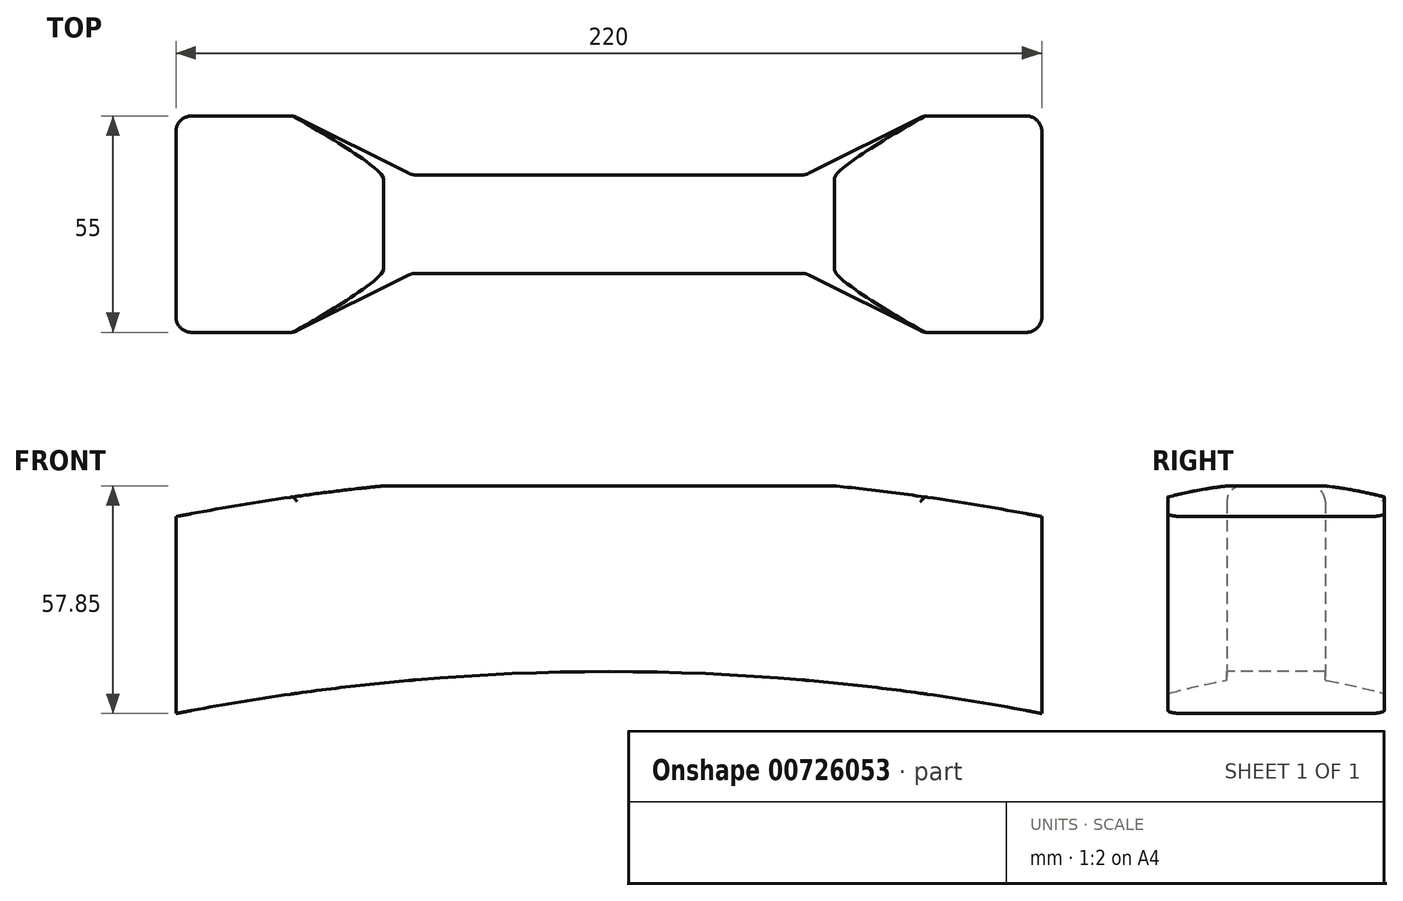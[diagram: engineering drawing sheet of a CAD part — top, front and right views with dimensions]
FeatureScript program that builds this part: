
annotation { "Feature Type Name" : "Feature", "Feature Type Description" : "" }
export const myFeature = defineFeature(function(context is Context, id is Id, definition is map)
    precondition{}
    {
        {
            var Q0;
            Q0=qCreatedBy(makeId("Top.planeOp"),FACE);
            var sketch = newSketch(context, id + "F0", { "sketchPlane" : qUnion([Q0])});
            skPoint(sketch, "E0.middle", {"position": v(0, 0) * mm});
            skPoint(sketch, "E0.left.end.orphan", {"position": v(50, 17.5) * mm});
            skPoint(sketch, "E1.orphan", {"position": v(50, -17.5) * mm});
            skLineSegment(sketch, "E2.0", {"start": v(-80, 27.5) * mm, "end": v(-110, 27.5) * mm});
            skLineSegment(sketch, "E3.0", {"start": v(-80, -27.5) * mm, "end": v(-110, -27.5) * mm});
            skLineSegment(sketch, "E4", {"start": v(-110, 27.5) * mm, "end": v(-110, -27.5) * mm});
            skPoint(sketch, "E5.orphan", {"position": v(-50, 27.5) * mm});
            skLineSegment(sketch, "E6.0", {"start": v(0, -12.5) * mm, "end": v(-50, -12.5) * mm});
            skLineSegment(sketch, "E7.0", {"start": v(0, 12.5) * mm, "end": v(-50, 12.5) * mm});
            skPoint(sketch, "E8.orphan", {"position": v(0, -17.5) * mm});
            skPoint(sketch, "E9.orphan", {"position": v(0, 17.5) * mm});
            skPoint(sketch, "E10.start.orphan", {"position": v(-50, -17.5) * mm});
            skPoint(sketch, "E11.end.orphan", {"position": v(-50, 17.5) * mm});
            skLineSegment(sketch, "E12", {"start": v(-80, -27.5) * mm, "end": v(-50, -12.5) * mm});
            skLineSegment(sketch, "E13", {"start": v(-50, 12.5) * mm, "end": v(-80, 27.5) * mm});
            skLineSegment(sketch, "E14.MirrorCS", {"start": v(80, -27.5) * mm, "end": v(50, -12.5) * mm});
            skLineSegment(sketch, "E15.MirrorCS", {"start": v(80, -27.5) * mm, "end": v(110, -27.5) * mm});
            skLineSegment(sketch, "E16.MirrorCS", {"start": v(0, -12.5) * mm, "end": v(50, -12.5) * mm});
            skLineSegment(sketch, "E17.MirrorCS", {"start": v(0, 12.5) * mm, "end": v(50, 12.5) * mm});
            skLineSegment(sketch, "E18.MirrorCS", {"start": v(50, 12.5) * mm, "end": v(80, 27.5) * mm});
            skLineSegment(sketch, "E19.MirrorCS", {"start": v(110, 27.5) * mm, "end": v(110, -27.5) * mm});
            skLineSegment(sketch, "E20.MirrorCS", {"start": v(80, 27.5) * mm, "end": v(110, 27.5) * mm});
            skSolve(sketch);
        }
        {
            var Q0;
            Q0=makeQuery(id+"F0.imprint","IMPRINT",FACE,{"disambiguationData":[TD([[makeQuery(id+"F0.imprint","IMPRINT",EDGE,{"derivedFrom":sQuery(id+"F0.wireOp",EDGE,"E2.0")}),1.0]])]});
            extrude(context, id + "F1", {"entities" : qUnion([Q0]), "depth" : 100 * mm, "offsetDistance" : 25 * mm});
        }
        {
            var Q0;
            Q0=makeQuery(id+"F1.opExtrude","SWEPT_FACE",FACE,{"disambiguationData":[OSD([sQuery(id+"F0.wireOp",EDGE,"E3.0")])]});
            var sketch = newSketch(context, id + "F2", { "sketchPlane" : qUnion([Q0])});
            skPoint(sketch, "E21.orphan", {"position": v(125.12, 0) * mm});
            skLineSegment(sketch, "E22.left", {"start": v(150, 32.82) * mm, "end": v(150, 82.82) * mm});
            skLineSegment(sketch, "E22.right", {"start": v(-150, 32.82) * mm, "end": v(-150, 82.82) * mm});
            skPoint(sketch, "E22.middle", {"position": v(0, 57.82) * mm});
            skArc(sketch, "E23", {"start": v(8.21, 102.82) * mm, "mid": v(0, 102.88) * mm, "end": v(-8.21, 102.82) * mm});
            skArc(sketch, "E24", {"start": v(150, 82.82) * mm, "mid": v(75.67, 97.84) * mm, "end": v(0, 102.88) * mm});
            skLineSegment(sketch, "E25", {"start": v(0, 57.82) * mm, "end": v(0, 52.82) * mm});
            skPoint(sketch, "E26.orphan", {"position": v(-150, 12.82) * mm});
            skPoint(sketch, "E27.0.start.orphan", {"position": v(150, 12.82) * mm});
            skPoint(sketch, "E28.orphan", {"position": v(0, 12.82) * mm});
            skArc(sketch, "E29", {"start": v(150, 32.82) * mm, "mid": v(0, 52.82) * mm, "end": v(-150, 32.82) * mm});
            skPoint(sketch, "E30.start.orphan", {"position": v(0, 102.88) * mm});
            skArc(sketch, "E31.trimOffspring", {"start": v(-8.21, 102.82) * mm, "mid": v(-79.74, 97.28) * mm, "end": v(-150, 82.82) * mm});
            skPoint(sketch, "E32.orphan", {"position": v(0, 32.82) * mm});
            skSolve(sketch);
        }
        {
            var Q0;
            Q0 = qSketchRegion(id + "F2", true);
            extrude(context, id + "F3", {"entities" : qUnion([Q0]), "operationType" : NewBodyOperationType.INTERSECT, "oppositeDirection" : true, "depth" : 185 * mm, "offsetDistance" : 25 * mm});
        }
        {
            var Q0;
            Q0=makeQuery(id+"F1.opExtrude","CAP_EDGE",EDGE,{"disambiguationData":[OSD([sQuery(id+"F0.wireOp",EDGE,"E7.0"),sQuery(id+"F0.wireOp",EDGE,"E17.MirrorCS")])],"isStart":false});
            var Q1;
            Q1=makeQuery(id+"F3.boolean.opBoolean","INTERSECT",EDGE,{"derivedFrom":[makeQuery(id+"F1.opExtrude","SWEPT_FACE",FACE,{"disambiguationData":[OSD([sQuery(id+"F0.wireOp",EDGE,"E18.MirrorCS")])]}),makeQuery(id+"F3.boolean.toolComplement.opBoolean","COPY",FACE,{"derivedFrom":makeQuery(id+"F3.opExtrude","SWEPT_FACE",FACE,{"disambiguationData":[OSD([sQuery(id+"F2.wireOp",EDGE,"E23"),sQuery(id+"F2.wireOp",EDGE,"E24"),sQuery(id+"F2.wireOp",EDGE,"E31.trimOffspring")])]})})]});
            var Q2;
            Q2=makeQuery(id+"F1.opExtrude","CAP_EDGE",EDGE,{"disambiguationData":[OSD([sQuery(id+"F0.wireOp",EDGE,"E18.MirrorCS")])],"isStart":false});
            var Q3;
            Q3=makeQuery(id+"F1.opExtrude","SWEPT_EDGE",EDGE,{"disambiguationData":[OSD([sQuery(id+"F0.wireOp",EDGE,"E17.MirrorCS"),sQuery(id+"F0.wireOp",EDGE,"E18.MirrorCS")])]});
            var Q4;
            Q4=makeQuery(id+"F1.opExtrude","SWEPT_EDGE",EDGE,{"disambiguationData":[OSD([sQuery(id+"F0.wireOp",EDGE,"E18.MirrorCS"),sQuery(id+"F0.wireOp",EDGE,"E20.MirrorCS")])]});
            var Q5;
            Q5=makeQuery(id+"F3.boolean.opBoolean","INTERSECT",EDGE,{"derivedFrom":[makeQuery(id+"F1.opExtrude","SWEPT_FACE",FACE,{"disambiguationData":[OSD([sQuery(id+"F0.wireOp",EDGE,"E20.MirrorCS")])]}),makeQuery(id+"F3.boolean.toolComplement.opBoolean","COPY",FACE,{"derivedFrom":makeQuery(id+"F3.opExtrude","SWEPT_FACE",FACE,{"disambiguationData":[OSD([sQuery(id+"F2.wireOp",EDGE,"E23"),sQuery(id+"F2.wireOp",EDGE,"E24"),sQuery(id+"F2.wireOp",EDGE,"E31.trimOffspring")])]})})]});
            var Q6;
            Q6=makeQuery(id+"F1.opExtrude","SWEPT_EDGE",EDGE,{"disambiguationData":[OSD([sQuery(id+"F0.wireOp",EDGE,"E19.MirrorCS"),sQuery(id+"F0.wireOp",EDGE,"E20.MirrorCS")])]});
            var Q7;
            Q7=makeQuery(id+"F3.boolean.opBoolean","INTERSECT",EDGE,{"derivedFrom":[makeQuery(id+"F1.opExtrude","SWEPT_FACE",FACE,{"disambiguationData":[OSD([sQuery(id+"F0.wireOp",EDGE,"E19.MirrorCS")])]}),makeQuery(id+"F3.boolean.toolComplement.opBoolean","COPY",FACE,{"derivedFrom":makeQuery(id+"F3.opExtrude","SWEPT_FACE",FACE,{"disambiguationData":[OSD([sQuery(id+"F2.wireOp",EDGE,"E23"),sQuery(id+"F2.wireOp",EDGE,"E24"),sQuery(id+"F2.wireOp",EDGE,"E31.trimOffspring")])]})})]});
            var Q8;
            Q8=makeQuery(id+"F3.boolean.opBoolean","INTERSECT",EDGE,{"derivedFrom":[makeQuery(id+"F1.opExtrude","SWEPT_FACE",FACE,{"disambiguationData":[OSD([sQuery(id+"F0.wireOp",EDGE,"E19.MirrorCS")])]}),makeQuery(id+"F3.boolean.toolComplement.opBoolean","COPY",FACE,{"derivedFrom":makeQuery(id+"F3.opExtrude","SWEPT_FACE",FACE,{"disambiguationData":[OSD([sQuery(id+"F2.wireOp",EDGE,"E29")])]})})]});
            var Q9;
            Q9=makeQuery(id+"F1.opExtrude","SWEPT_EDGE",EDGE,{"disambiguationData":[OSD([sQuery(id+"F0.wireOp",EDGE,"E15.MirrorCS"),sQuery(id+"F0.wireOp",EDGE,"E19.MirrorCS")])]});
            var Q10;
            Q10=makeQuery(id+"F3.boolean.opBoolean","INTERSECT",EDGE,{"derivedFrom":[makeQuery(id+"F1.opExtrude","SWEPT_FACE",FACE,{"disambiguationData":[OSD([sQuery(id+"F0.wireOp",EDGE,"E20.MirrorCS")])]}),makeQuery(id+"F3.boolean.toolComplement.opBoolean","COPY",FACE,{"derivedFrom":makeQuery(id+"F3.opExtrude","SWEPT_FACE",FACE,{"disambiguationData":[OSD([sQuery(id+"F2.wireOp",EDGE,"E29")])]})})]});
            var Q11;
            Q11=makeQuery(id+"F3.boolean.opBoolean","INTERSECT",EDGE,{"derivedFrom":[makeQuery(id+"F1.opExtrude","SWEPT_FACE",FACE,{"disambiguationData":[OSD([sQuery(id+"F0.wireOp",EDGE,"E18.MirrorCS")])]}),makeQuery(id+"F3.boolean.toolComplement.opBoolean","COPY",FACE,{"derivedFrom":makeQuery(id+"F3.opExtrude","SWEPT_FACE",FACE,{"disambiguationData":[OSD([sQuery(id+"F2.wireOp",EDGE,"E29")])]})})]});
            var Q12;
            Q12=makeQuery(id+"F3.boolean.opBoolean","INTERSECT",EDGE,{"derivedFrom":[makeQuery(id+"F1.opExtrude","SWEPT_FACE",FACE,{"disambiguationData":[OSD([sQuery(id+"F0.wireOp",EDGE,"E7.0"),sQuery(id+"F0.wireOp",EDGE,"E17.MirrorCS")])]}),makeQuery(id+"F3.boolean.toolComplement.opBoolean","COPY",FACE,{"derivedFrom":makeQuery(id+"F3.opExtrude","SWEPT_FACE",FACE,{"disambiguationData":[OSD([sQuery(id+"F2.wireOp",EDGE,"E29")])]})})]});
            var Q13;
            Q13=makeQuery(id+"F1.opExtrude","SWEPT_EDGE",EDGE,{"disambiguationData":[OSD([sQuery(id+"F0.wireOp",EDGE,"E7.0"),sQuery(id+"F0.wireOp",EDGE,"E13")])]});
            var Q14;
            Q14=makeQuery(id+"F3.boolean.opBoolean","INTERSECT",EDGE,{"derivedFrom":[makeQuery(id+"F1.opExtrude","SWEPT_FACE",FACE,{"disambiguationData":[OSD([sQuery(id+"F0.wireOp",EDGE,"E13")])]}),makeQuery(id+"F3.boolean.toolComplement.opBoolean","COPY",FACE,{"derivedFrom":makeQuery(id+"F3.opExtrude","SWEPT_FACE",FACE,{"disambiguationData":[OSD([sQuery(id+"F2.wireOp",EDGE,"E23"),sQuery(id+"F2.wireOp",EDGE,"E24"),sQuery(id+"F2.wireOp",EDGE,"E31.trimOffspring")])]})})]});
            var Q15;
            Q15=makeQuery(id+"F1.opExtrude","CAP_EDGE",EDGE,{"disambiguationData":[OSD([sQuery(id+"F0.wireOp",EDGE,"E13")])],"isStart":false});
            var Q16;
            Q16=makeQuery(id+"F3.boolean.opBoolean","INTERSECT",EDGE,{"derivedFrom":[makeQuery(id+"F1.opExtrude","SWEPT_FACE",FACE,{"disambiguationData":[OSD([sQuery(id+"F0.wireOp",EDGE,"E13")])]}),makeQuery(id+"F3.boolean.toolComplement.opBoolean","COPY",FACE,{"derivedFrom":makeQuery(id+"F3.opExtrude","SWEPT_FACE",FACE,{"disambiguationData":[OSD([sQuery(id+"F2.wireOp",EDGE,"E29")])]})})]});
            var Q17;
            Q17=makeQuery(id+"F1.opExtrude","SWEPT_EDGE",EDGE,{"disambiguationData":[OSD([sQuery(id+"F0.wireOp",EDGE,"E2.0"),sQuery(id+"F0.wireOp",EDGE,"E13")])]});
            var Q18;
            Q18=makeQuery(id+"F3.boolean.opBoolean","INTERSECT",EDGE,{"derivedFrom":[makeQuery(id+"F1.opExtrude","SWEPT_FACE",FACE,{"disambiguationData":[OSD([sQuery(id+"F0.wireOp",EDGE,"E2.0")])]}),makeQuery(id+"F3.boolean.toolComplement.opBoolean","COPY",FACE,{"derivedFrom":makeQuery(id+"F3.opExtrude","SWEPT_FACE",FACE,{"disambiguationData":[OSD([sQuery(id+"F2.wireOp",EDGE,"E23"),sQuery(id+"F2.wireOp",EDGE,"E24"),sQuery(id+"F2.wireOp",EDGE,"E31.trimOffspring")])]})})]});
            var Q19;
            Q19=makeQuery(id+"F3.boolean.opBoolean","INTERSECT",EDGE,{"derivedFrom":[makeQuery(id+"F1.opExtrude","SWEPT_FACE",FACE,{"disambiguationData":[OSD([sQuery(id+"F0.wireOp",EDGE,"E2.0")])]}),makeQuery(id+"F3.boolean.toolComplement.opBoolean","COPY",FACE,{"derivedFrom":makeQuery(id+"F3.opExtrude","SWEPT_FACE",FACE,{"disambiguationData":[OSD([sQuery(id+"F2.wireOp",EDGE,"E29")])]})})]});
            var Q20;
            Q20=makeQuery(id+"F1.opExtrude","SWEPT_EDGE",EDGE,{"disambiguationData":[OSD([sQuery(id+"F0.wireOp",EDGE,"E2.0"),sQuery(id+"F0.wireOp",EDGE,"E4")])]});
            var Q21;
            Q21=makeQuery(id+"F3.boolean.opBoolean","INTERSECT",EDGE,{"derivedFrom":[makeQuery(id+"F1.opExtrude","SWEPT_FACE",FACE,{"disambiguationData":[OSD([sQuery(id+"F0.wireOp",EDGE,"E4")])]}),makeQuery(id+"F3.boolean.toolComplement.opBoolean","COPY",FACE,{"derivedFrom":makeQuery(id+"F3.opExtrude","SWEPT_FACE",FACE,{"disambiguationData":[OSD([sQuery(id+"F2.wireOp",EDGE,"E23"),sQuery(id+"F2.wireOp",EDGE,"E24"),sQuery(id+"F2.wireOp",EDGE,"E31.trimOffspring")])]})})]});
            var Q22;
            Q22=makeQuery(id+"F3.boolean.opBoolean","INTERSECT",EDGE,{"derivedFrom":[makeQuery(id+"F1.opExtrude","SWEPT_FACE",FACE,{"disambiguationData":[OSD([sQuery(id+"F0.wireOp",EDGE,"E4")])]}),makeQuery(id+"F3.boolean.toolComplement.opBoolean","COPY",FACE,{"derivedFrom":makeQuery(id+"F3.opExtrude","SWEPT_FACE",FACE,{"disambiguationData":[OSD([sQuery(id+"F2.wireOp",EDGE,"E29")])]})})]});
            var Q23;
            Q23=makeQuery(id+"F1.opExtrude","SWEPT_EDGE",EDGE,{"disambiguationData":[OSD([sQuery(id+"F0.wireOp",EDGE,"E3.0"),sQuery(id+"F0.wireOp",EDGE,"E4")])]});
            var Q24;
            {var subQ0=sQuery(id+"F2.wireOp",EDGE,"E31.trimOffspring");var subQ1=sQuery(id+"F2.wireOp",EDGE,"E24");var subQ2=sQuery(id+"F2.wireOp",EDGE,"E23");Q24=makeQuery(id+"F3.boolean.opBoolean","COPY",EDGE,{"disambiguationData":[topologyDisambiguationEdgeConnected([makeQuery(id+"F1.opExtrude","SWEPT_FACE",FACE,{"disambiguationData":[OSD([sQuery(id+"F0.wireOp",EDGE,"E3.0")])]})])],"derivedFrom":makeQuery(id+"F3.boolean.toolComplement.opBoolean","COPY",EDGE,{"derivedFrom":makeQuery(id+"F3.opExtrude","CAP_EDGE",EDGE,{"disambiguationData":[OSD([subQ2,subQ1,subQ0])],"isStart":true})})});}
            var Q25;
            Q25=makeQuery(id+"F3.boolean.opBoolean","INTERSECT",EDGE,{"derivedFrom":[makeQuery(id+"F1.opExtrude","SWEPT_FACE",FACE,{"disambiguationData":[OSD([sQuery(id+"F0.wireOp",EDGE,"E12")])]}),makeQuery(id+"F3.boolean.toolComplement.opBoolean","COPY",FACE,{"derivedFrom":makeQuery(id+"F3.opExtrude","SWEPT_FACE",FACE,{"disambiguationData":[OSD([sQuery(id+"F2.wireOp",EDGE,"E23"),sQuery(id+"F2.wireOp",EDGE,"E24"),sQuery(id+"F2.wireOp",EDGE,"E31.trimOffspring")])]})})]});
            var Q26;
            Q26=makeQuery(id+"F1.opExtrude","CAP_EDGE",EDGE,{"disambiguationData":[OSD([sQuery(id+"F0.wireOp",EDGE,"E12")])],"isStart":false});
            var Q27;
            Q27=makeQuery(id+"F1.opExtrude","CAP_EDGE",EDGE,{"disambiguationData":[OSD([sQuery(id+"F0.wireOp",EDGE,"E6.0"),sQuery(id+"F0.wireOp",EDGE,"E16.MirrorCS")])],"isStart":false});
            var Q28;
            Q28=makeQuery(id+"F1.opExtrude","SWEPT_EDGE",EDGE,{"disambiguationData":[OSD([sQuery(id+"F0.wireOp",EDGE,"E14.MirrorCS"),sQuery(id+"F0.wireOp",EDGE,"E16.MirrorCS")])]});
            var Q29;
            Q29=makeQuery(id+"F3.boolean.opBoolean","INTERSECT",EDGE,{"derivedFrom":[makeQuery(id+"F1.opExtrude","SWEPT_FACE",FACE,{"disambiguationData":[OSD([sQuery(id+"F0.wireOp",EDGE,"E14.MirrorCS")])]}),makeQuery(id+"F3.boolean.toolComplement.opBoolean","COPY",FACE,{"derivedFrom":makeQuery(id+"F3.opExtrude","SWEPT_FACE",FACE,{"disambiguationData":[OSD([sQuery(id+"F2.wireOp",EDGE,"E23"),sQuery(id+"F2.wireOp",EDGE,"E24"),sQuery(id+"F2.wireOp",EDGE,"E31.trimOffspring")])]})})]});
            var Q30;
            Q30=makeQuery(id+"F1.opExtrude","CAP_EDGE",EDGE,{"disambiguationData":[OSD([sQuery(id+"F0.wireOp",EDGE,"E14.MirrorCS")])],"isStart":false});
            var Q31;
            Q31=makeQuery(id+"F1.opExtrude","SWEPT_EDGE",EDGE,{"disambiguationData":[OSD([sQuery(id+"F0.wireOp",EDGE,"E14.MirrorCS"),sQuery(id+"F0.wireOp",EDGE,"E15.MirrorCS")])]});
            var Q32;
            {var subQ0=sQuery(id+"F2.wireOp",EDGE,"E31.trimOffspring");var subQ1=sQuery(id+"F2.wireOp",EDGE,"E24");var subQ2=sQuery(id+"F2.wireOp",EDGE,"E23");Q32=makeQuery(id+"F3.boolean.opBoolean","COPY",EDGE,{"disambiguationData":[topologyDisambiguationEdgeConnected([makeQuery(id+"F1.opExtrude","SWEPT_FACE",FACE,{"disambiguationData":[OSD([sQuery(id+"F0.wireOp",EDGE,"E15.MirrorCS")])]})])],"derivedFrom":makeQuery(id+"F3.boolean.toolComplement.opBoolean","COPY",EDGE,{"derivedFrom":makeQuery(id+"F3.opExtrude","CAP_EDGE",EDGE,{"disambiguationData":[OSD([subQ2,subQ1,subQ0])],"isStart":true})})});}
            var Q33;
            Q33=makeQuery(id+"F3.boolean.opBoolean","INTERSECT",EDGE,{"derivedFrom":[makeQuery(id+"F1.opExtrude","SWEPT_FACE",FACE,{"disambiguationData":[OSD([sQuery(id+"F0.wireOp",EDGE,"E14.MirrorCS")])]}),makeQuery(id+"F3.boolean.toolComplement.opBoolean","COPY",FACE,{"derivedFrom":makeQuery(id+"F3.opExtrude","SWEPT_FACE",FACE,{"disambiguationData":[OSD([sQuery(id+"F2.wireOp",EDGE,"E29")])]})})]});
            var Q34;
            {var subQ0=sQuery(id+"F2.wireOp",EDGE,"E29");Q34=makeQuery(id+"F3.boolean.opBoolean","COPY",EDGE,{"disambiguationData":[topologyDisambiguationEdgeConnected([makeQuery(id+"F1.opExtrude","SWEPT_FACE",FACE,{"disambiguationData":[OSD([sQuery(id+"F0.wireOp",EDGE,"E15.MirrorCS")])]})])],"derivedFrom":makeQuery(id+"F3.boolean.toolComplement.opBoolean","COPY",EDGE,{"derivedFrom":makeQuery(id+"F3.opExtrude","CAP_EDGE",EDGE,{"disambiguationData":[OSD([subQ0])],"isStart":true})})});}
            var Q35;
            Q35=makeQuery(id+"F3.boolean.opBoolean","INTERSECT",EDGE,{"derivedFrom":[makeQuery(id+"F1.opExtrude","SWEPT_FACE",FACE,{"disambiguationData":[OSD([sQuery(id+"F0.wireOp",EDGE,"E6.0"),sQuery(id+"F0.wireOp",EDGE,"E16.MirrorCS")])]}),makeQuery(id+"F3.boolean.toolComplement.opBoolean","COPY",FACE,{"derivedFrom":makeQuery(id+"F3.opExtrude","SWEPT_FACE",FACE,{"disambiguationData":[OSD([sQuery(id+"F2.wireOp",EDGE,"E29")])]})})]});
            var Q36;
            Q36=makeQuery(id+"F3.boolean.opBoolean","INTERSECT",EDGE,{"derivedFrom":[makeQuery(id+"F1.opExtrude","SWEPT_FACE",FACE,{"disambiguationData":[OSD([sQuery(id+"F0.wireOp",EDGE,"E12")])]}),makeQuery(id+"F3.boolean.toolComplement.opBoolean","COPY",FACE,{"derivedFrom":makeQuery(id+"F3.opExtrude","SWEPT_FACE",FACE,{"disambiguationData":[OSD([sQuery(id+"F2.wireOp",EDGE,"E29")])]})})]});
            var Q37;
            Q37=makeQuery(id+"F1.opExtrude","SWEPT_EDGE",EDGE,{"disambiguationData":[OSD([sQuery(id+"F0.wireOp",EDGE,"E3.0"),sQuery(id+"F0.wireOp",EDGE,"E12")])]});
            var Q38;
            {var subQ0=sQuery(id+"F2.wireOp",EDGE,"E29");Q38=makeQuery(id+"F3.boolean.opBoolean","COPY",EDGE,{"disambiguationData":[topologyDisambiguationEdgeConnected([makeQuery(id+"F1.opExtrude","SWEPT_FACE",FACE,{"disambiguationData":[OSD([sQuery(id+"F0.wireOp",EDGE,"E3.0")])]})])],"derivedFrom":makeQuery(id+"F3.boolean.toolComplement.opBoolean","COPY",EDGE,{"derivedFrom":makeQuery(id+"F3.opExtrude","CAP_EDGE",EDGE,{"disambiguationData":[OSD([subQ0])],"isStart":true})})});}
            var Q39;
            Q39=makeQuery(id+"F1.opExtrude","SWEPT_EDGE",EDGE,{"disambiguationData":[OSD([sQuery(id+"F0.wireOp",EDGE,"E6.0"),sQuery(id+"F0.wireOp",EDGE,"E12")])]});
            var Q40;
            Q40=makeQuery(id+"F3.boolean.opBoolean","INTERSECT",EDGE,{"disambiguationData":[OD(1.0)],"derivedFrom":[makeQuery(id+"F1.opExtrude","CAP_FACE",FACE,{"disambiguationData":[OSD([sQuery(id+"F0.wireOp",EDGE,"E2.0"),sQuery(id+"F0.wireOp",EDGE,"E3.0"),sQuery(id+"F0.wireOp",EDGE,"E4"),sQuery(id+"F0.wireOp",EDGE,"E6.0"),sQuery(id+"F0.wireOp",EDGE,"E7.0"),sQuery(id+"F0.wireOp",EDGE,"E12"),sQuery(id+"F0.wireOp",EDGE,"E13"),sQuery(id+"F0.wireOp",EDGE,"E14.MirrorCS"),sQuery(id+"F0.wireOp",EDGE,"E15.MirrorCS"),sQuery(id+"F0.wireOp",EDGE,"E16.MirrorCS"),sQuery(id+"F0.wireOp",EDGE,"E17.MirrorCS"),sQuery(id+"F0.wireOp",EDGE,"E18.MirrorCS"),sQuery(id+"F0.wireOp",EDGE,"E19.MirrorCS"),sQuery(id+"F0.wireOp",EDGE,"E20.MirrorCS")])],"isStart":false}),makeQuery(id+"F3.boolean.toolComplement.opBoolean","COPY",FACE,{"derivedFrom":makeQuery(id+"F3.opExtrude","SWEPT_FACE",FACE,{"disambiguationData":[OSD([sQuery(id+"F2.wireOp",EDGE,"E23"),sQuery(id+"F2.wireOp",EDGE,"E24"),sQuery(id+"F2.wireOp",EDGE,"E31.trimOffspring")])]})})]});
            var Q41;
            Q41=makeQuery(id+"F3.boolean.opBoolean","INTERSECT",EDGE,{"disambiguationData":[OD(0.0)],"derivedFrom":[makeQuery(id+"F1.opExtrude","CAP_FACE",FACE,{"disambiguationData":[OSD([sQuery(id+"F0.wireOp",EDGE,"E2.0"),sQuery(id+"F0.wireOp",EDGE,"E3.0"),sQuery(id+"F0.wireOp",EDGE,"E4"),sQuery(id+"F0.wireOp",EDGE,"E6.0"),sQuery(id+"F0.wireOp",EDGE,"E7.0"),sQuery(id+"F0.wireOp",EDGE,"E12"),sQuery(id+"F0.wireOp",EDGE,"E13"),sQuery(id+"F0.wireOp",EDGE,"E14.MirrorCS"),sQuery(id+"F0.wireOp",EDGE,"E15.MirrorCS"),sQuery(id+"F0.wireOp",EDGE,"E16.MirrorCS"),sQuery(id+"F0.wireOp",EDGE,"E17.MirrorCS"),sQuery(id+"F0.wireOp",EDGE,"E18.MirrorCS"),sQuery(id+"F0.wireOp",EDGE,"E19.MirrorCS"),sQuery(id+"F0.wireOp",EDGE,"E20.MirrorCS")])],"isStart":false}),makeQuery(id+"F3.boolean.toolComplement.opBoolean","COPY",FACE,{"derivedFrom":makeQuery(id+"F3.opExtrude","SWEPT_FACE",FACE,{"disambiguationData":[OSD([sQuery(id+"F2.wireOp",EDGE,"E23"),sQuery(id+"F2.wireOp",EDGE,"E24"),sQuery(id+"F2.wireOp",EDGE,"E31.trimOffspring")])]})})]});
            fillet(context, id + "F4", {"entities" : qUnion([Q0, Q1, Q2, Q3, Q4, Q5, Q6, Q7, Q8, Q9, Q10, Q11, Q12, Q13, Q14, Q15, Q16, Q17, Q18, Q19, Q20, Q21, Q22, Q23, Q24, Q25, Q26, Q27, Q28, Q29, Q30, Q31, Q32, Q33, Q34, Q35, Q36, Q37, Q38, Q39, Q40, Q41]), "radius" : 4 * mm, "tangentPropagation" : true, "allowEdgeOverflow" : false});
        }
    });
